# Revit family: Door_Raised-Panel-Double
name_source: partatom
category: Doors
units: mm (PartAtom-declared; Revit-internal decimal feet)

## family parameters
Always vertical = Yes
Classification Number = 23.30.10.11.17
Cut with Voids When Loaded = No
Host = Wall
Room Calculation Point = No
Shared = No

## types (1)
- Custom
    Assembly Code = C1020100
    Building Codes = http://www.iccsafe.org
    CasingMaterial = ARCAT - Wood - Cherry_Domestic
    CladdingMaterial = ARCAT - Metal - Aluminum_0.032" - Patina
    Construction Details = http://www.arcat.com
    Description = Interior Inswing Double Door
    Door Leaf Count = 2
    ENERGYSTAR Rating = North/Central
    Expected Lifespan (Years) = 15
    Fax = (203) 929-2444
    Fire Rating = 1 hour
    Function = Interior
    Green Building-LEED = http://www.usgbc.org
    HandleHeight = 3' - 0"
    Height = 7' - 0"
    Installation Phase = Millwork
    JambMaterial = ARCAT - Wood - Pine_Northern White
    JambThickness = 0' - 0 3/4"
    Keynote = 08200
    LateralClearance = 0' - 1 1/2"
    Leafcheck = 2
    Maintenance Schedule (Months) = 36
    Manufacturer = Generic
    Model = Generic
    PanelCheck = 6
    PanelThickness = 0' - 0 27/32"
    PnViz2 = Yes
    PnViz3 = Yes
    PnViz4 = Yes
    Product Data = http://www.arcat.com
    Product Properties = http://www.arcat.com
    R_Value = 0
    Rail-Bottom = 0' - 10"
    Rail-Center = 0' - 4"
    Rail-Top = 0' - 4"
    Raised Panel Count = 6
    Rough Height = 7' - 1 1/2"
    Rough Opening Clearance = 0' - 0 3/4"
    Rough Width = 4' - 3"
    SHGC = 0.54
    SlabMaterial = ARCAT - Wood - Pine_Northern White
    SlabThickness = 0' - 2 1/2"
    Specification = http://www.arcat.com
    Stile = 0' - 4"
    SwingArcViz = Yes
    Test Data = http://www.aamanet.org
    Thickness = 0' - 2 1/2"
    Total Width = 4' - 0"
    Type Comments = Interior
    URL = http://www.arcat.com
    U_Factor = 0.39
    Wall Closure = By host
    Warranty Duration (Years) = 10
    Width = 2' - 0"

## geometry (parser evidence)
native form markers: Sweep x8
no freeform markers — native parametric forms only
